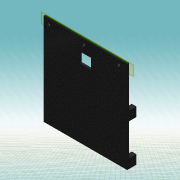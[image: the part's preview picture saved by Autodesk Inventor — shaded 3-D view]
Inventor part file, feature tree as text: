
AUTODESK INVENTOR PART (.ipt)
format: ipt  version: 2019 (Build 230136000, 136)  size: 227,840 bytes
history: native  units: mm
features: sketch x11, extrude x8, reference x8, other x3, plane x1
ambient origin geometry x8: Origin, YZ Plane, XZ Plane, XY Plane, X Axis, Y Axis, Z Axis, Center Point
bodies: Solid1 (feature_tree)
feature tree (31):
  plane  "Work Plane1"
  extrude  "Extrusion1"  Depth=100.0mm
  sketch  "Sketch2"  dims[d2=1.0mm d3=1.0mm]
  sketch  "Sketch3"  dims[d4=1.0mm d5=2.0mm d6=0.0mm]
  extrude  "Extrusion2"  Depth=1.0mm
  extrude  "Extrusion3"  Depth=2.0mm TaperAngle=0.0deg
  extrude  "Extrusion4"  Depth=4.0mm
  extrude  "Extrusion5"  Depth=8.0mm
  extrude  "Extrusion6"  Depth=8.0mm
  sketch  "Sketch9"  dims[d20=5.0mm d21=0.0mm]
  extrude  "Extrusion7"  Depth=8.0mm
  extrude  "Extrusion8"  Depth=10.0mm
  sketch  "Sketch1"  dims[d0=91.0mm d1=100.0mm]
  reference  "Reference1"
  reference  "Reference2"
  reference  "Reference3"
  reference  "Reference4"
  reference  "Reference5"
  reference  "Reference6"
  reference  "Reference7"
  reference  "Reference8"
  sketch  "Sketch4"  dims[d8=1.5mm d9=4.0mm]
  sketch  "Sketch5"  dims[d10=5.0mm d11=8.0mm]
  sketch  "Sketch6"  dims[d12=10.0mm d13=8.0mm]
  sketch  "Sketch7"  dims[d14=5.0mm d15=0.0mm d16=8.0mm]
  sketch  "Sketch8"  dims[d17=10.0mm d19=1.5mm]
  sketch  "Sketch10"  dims[d22=10.0mm]
  sketch  "Sketch11"  dims[d23=8.0mm d25=1.5mm d26=5.0mm d27=0.0mm d28=5.0mm d29=0.0mm d30=5.0mm d31=0.0mm d32=10.0mm d33=8.0mm d35=1.5mm d36=5.0mm d37=0.0mm d39=1.5mm d40=4.0mm d41=5.0mm d42=8.0mm d43=10.0mm d44=8.0mm d45=5.0mm d46=0.0mm]
  other  "Ensamblaje Reloj LCD 16x2.iam"
  other  "Down:1"
  other  "PCB Down:1"
